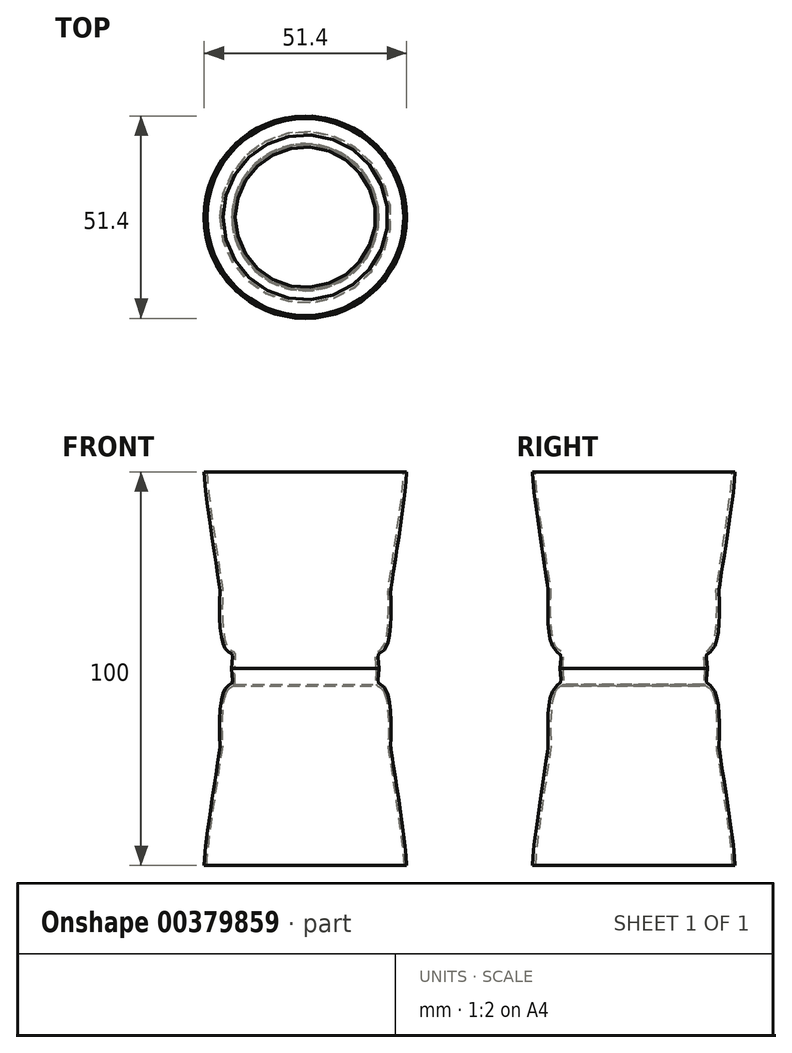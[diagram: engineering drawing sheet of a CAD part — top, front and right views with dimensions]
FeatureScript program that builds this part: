
annotation { "Feature Type Name" : "Feature", "Feature Type Description" : "" }
export const myFeature = defineFeature(function(context is Context, id is Id, definition is map)
    precondition{}
    {
        {
            var Q0;
            Q0=qCreatedBy(makeId("Front.planeOp"),FACE);
            var sketch = newSketch(context, id + "F0", { "sketchPlane" : qUnion([Q0])});
            skFitSpline(sketch, "E0", {"points": [v(-25, -50) * mm, v(-21, -20) * mm, v(-21, -19) * mm, v(-20, -6) * mm, v(-18, -4) * mm, v(-18, 0) * mm], "startDerivative": vector(0, 37.61) * mm, "endDerivative": vector(0, 41.38) * mm});
            skLineSegment(sketch, "E1", {"start": v(-25, -50) * mm, "end": v(0, -50) * mm, "construction": true});
            skLineSegment(sketch, "E2", {"start": v(0, -50) * mm, "end": v(0, 0) * mm, "construction": true});
            skLineSegment(sketch, "E3", {"start": v(0, 0) * mm, "end": v(-18, 0) * mm, "construction": true});
            skLineSegment(sketch, "E4", {"start": v(-18, -4) * mm, "end": v(0, -4) * mm, "construction": true});
            skLineSegment(sketch, "E5", {"start": v(-20, -6) * mm, "end": v(0, -6) * mm, "construction": true});
            skLineSegment(sketch, "E6", {"start": v(-21, -19) * mm, "end": v(0, -19) * mm, "construction": true});
            skLineSegment(sketch, "E7", {"start": v(-21, -20) * mm, "end": v(0, -20) * mm, "construction": true});
            skLineSegment(sketch, "E8", {"start": v(-25, -45) * mm, "end": v(0, -45) * mm, "construction": true});
            skLineSegment(sketch, "E9", {"start": v(-18, -2) * mm, "end": v(0, -2) * mm, "construction": true});
            skLineSegment(sketch, "E10", {"start": v(-18, -4) * mm, "end": v(-18, -4) * mm});
            skLineSegment(sketch, "E11", {"start": v(-18, -4) * mm, "end": v(-18, -50) * mm, "construction": true});
            skLineSegment(sketch, "E12", {"start": v(-18, -4) * mm, "end": v(-20, -6) * mm});
            skFitSpline(sketch, "E13.0", {"points": [v(-25.7, -50) * mm, v(-25.7, -49.58) * mm, v(-25.65, -48.57) * mm, v(-25.41, -45.87) * mm, v(-24.88, -41.48) * mm, v(-24.16, -36.39) * mm, v(-23.56, -32.31) * mm, v(-23.12, -29.35) * mm, v(-22.7, -26.6) * mm, v(-22.32, -24.14) * mm, v(-22, -22.1) * mm, v(-21.82, -20.81) * mm, v(-21.72, -20.1) * mm, v(-21.67, -19.73) * mm, v(-21.66, -19.55) * mm, v(-21.66, -19.5) * mm, v(-21.66, -19.43) * mm, v(-21.67, -19.33) * mm, v(-21.7, -19.13) * mm, v(-21.72, -18.76) * mm, v(-21.76, -18.1) * mm, v(-21.8, -16.99) * mm, v(-21.82, -15.32) * mm, v(-21.8, -13.44) * mm, v(-21.71, -11.47) * mm, v(-21.55, -9.54) * mm, v(-21.33, -8.05) * mm, v(-21.1, -6.99) * mm, v(-20.92, -6.39) * mm, v(-20.75, -5.95) * mm, v(-20.56, -5.54) * mm, v(-20.3, -5.1) * mm, v(-19.94, -4.67) * mm, v(-19.58, -4.34) * mm, v(-19.24, -4.1) * mm, v(-18.94, -3.9) * mm, v(-18.73, -3.76) * mm, v(-18.63, -3.67) * mm, v(-18.6, -3.63) * mm, v(-18.57, -3.6) * mm, v(-18.54, -3.52) * mm, v(-18.5, -3.34) * mm, v(-18.5, -3.06) * mm, v(-18.52, -2.7) * mm, v(-18.57, -2.15) * mm, v(-18.66, -1.29) * mm, v(-18.7, -0.45) * mm, v(-18.7, 0) * mm]});
            skLineSegment(sketch, "E14", {"start": v(-18.7, 0) * mm, "end": v(-18, 0) * mm});
            skLineSegment(sketch, "E15", {"start": v(-25.7, -50) * mm, "end": v(-25, -50) * mm});
            skFitSpline(sketch, "E16.MirrorCS", {"points": [v(-25, 50) * mm, v(-21, 20) * mm, v(-21, 19) * mm, v(-20, 6) * mm, v(-18, 4) * mm, v(-18, 0) * mm], "startDerivative": vector(0, -37.61) * mm, "endDerivative": vector(0, -41.38) * mm});
            skLineSegment(sketch, "E17", {"start": v(-25.7, -50) * mm, "end": v(-18, -50) * mm, "construction": true});
            skFitSpline(sketch, "E18.0", {"points": [v(-25.7, 50) * mm, v(-25.7, 49.58) * mm, v(-25.65, 48.57) * mm, v(-25.41, 45.87) * mm, v(-24.88, 41.48) * mm, v(-24.16, 36.39) * mm, v(-23.56, 32.31) * mm, v(-23.12, 29.35) * mm, v(-22.7, 26.6) * mm, v(-22.32, 24.14) * mm, v(-22, 22.1) * mm, v(-21.82, 20.81) * mm, v(-21.72, 20.1) * mm, v(-21.67, 19.73) * mm, v(-21.66, 19.55) * mm, v(-21.66, 19.5) * mm, v(-21.66, 19.43) * mm, v(-21.67, 19.33) * mm, v(-21.7, 19.13) * mm, v(-21.72, 18.76) * mm, v(-21.76, 18.1) * mm, v(-21.8, 16.99) * mm, v(-21.82, 15.32) * mm, v(-21.8, 13.44) * mm, v(-21.71, 11.47) * mm, v(-21.55, 9.54) * mm, v(-21.33, 8.05) * mm, v(-21.1, 6.99) * mm, v(-20.92, 6.39) * mm, v(-20.75, 5.95) * mm, v(-20.56, 5.54) * mm, v(-20.3, 5.1) * mm, v(-19.94, 4.67) * mm, v(-19.58, 4.34) * mm, v(-19.24, 4.1) * mm, v(-18.94, 3.9) * mm, v(-18.73, 3.76) * mm, v(-18.63, 3.67) * mm, v(-18.6, 3.63) * mm, v(-18.57, 3.6) * mm, v(-18.54, 3.52) * mm, v(-18.5, 3.34) * mm, v(-18.5, 3.06) * mm, v(-18.52, 2.7) * mm, v(-18.57, 2.15) * mm, v(-18.66, 1.29) * mm, v(-18.7, 0.45) * mm, v(-18.7, 0) * mm]});
            skLineSegment(sketch, "E19", {"start": v(-25.7, 50) * mm, "end": v(-25, 50) * mm});
            skLineSegment(sketch, "E20", {"start": v(-25.7, 50) * mm, "end": v(0, 50) * mm, "construction": true});
            skSolve(sketch);
        }
        {
            var Q0;
            Q0=makeQuery(id+"F0.imprint","IMPRINT",FACE,{"disambiguationData":[TD([[makeQuery(id+"F0.imprint","IMPRINT",EDGE,{"derivedFrom":sQuery(id+"F0.wireOp",EDGE,"E14")}),1.0]])]});
            var Q1;
            Q1=makeQuery(id+"F0.imprint","IMPRINT",FACE,{"disambiguationData":[TD([[makeQuery(id+"F0.imprint","IMPRINT",EDGE,{"derivedFrom":sQuery(id+"F0.wireOp",EDGE,"E13.0")}),-1.0]])]});
            var Q2;
            Q2=sQuery(id+"F0.wireOp",EDGE,"E2");
            revolve(context, id + "F1", {"entities" : qUnion([Q0, Q1]), "axis" : qUnion([Q2]), "revolveType" : RevolveType.FULL});
        }
    });
